# Revit family: 3456A_NX_Smart_Port
name_source: partatom
category: Communication Devices
units: mm (PartAtom-declared; Revit-internal decimal feet)

## family parameters
Cut with Voids When Loaded = No
Host = Face
Maintain Annotation Orientation = No
OmniClass Number = 23.85.80.11.27
OmniClass Title = Lighting Controls
Part Type = Normal
Room Calculation Point = No
Round Connector Dimension = Use Diameter
Shared = Yes

## types (1)
- 3456A_NX_Smart_Port
    Apparent Load = 0 VA
    Assembly Code = D5090
    Black Material = Paint -  Black Matte Textured
    Default Elevation = 48 "
    Description = The NX SmartPORT Module provides easy access to connect smart switch stations, motion detectors, and daylight sensors into a NX network system
    Featrues = Connects to the network through the NXHDI
Device Network Interface Module
• Four independent SmartPORT connectors, each with two
RJ45 connectors
• Compatible with all NX Smart Switch Stations, NX Occupancy
Sensors and NX Daylight Sensor
• Mounts to standard DIN rail
    Green Element = Plastic -  Green
    Manufacturer = NX Lighting Controls
    Model = NX SmartPORT Module
    Steel = Metal-Galvanized_Steel
    Type Comments = NX SmartPORT Module
    URL = https://www.currentlighting.com
    Voltage = 24 V
    Warranty = 5-Years Warranty
    White Element = Glass, White, High Luminance

## geometry (parser evidence)
native form markers: Sweep x2
no freeform markers — native parametric forms only
